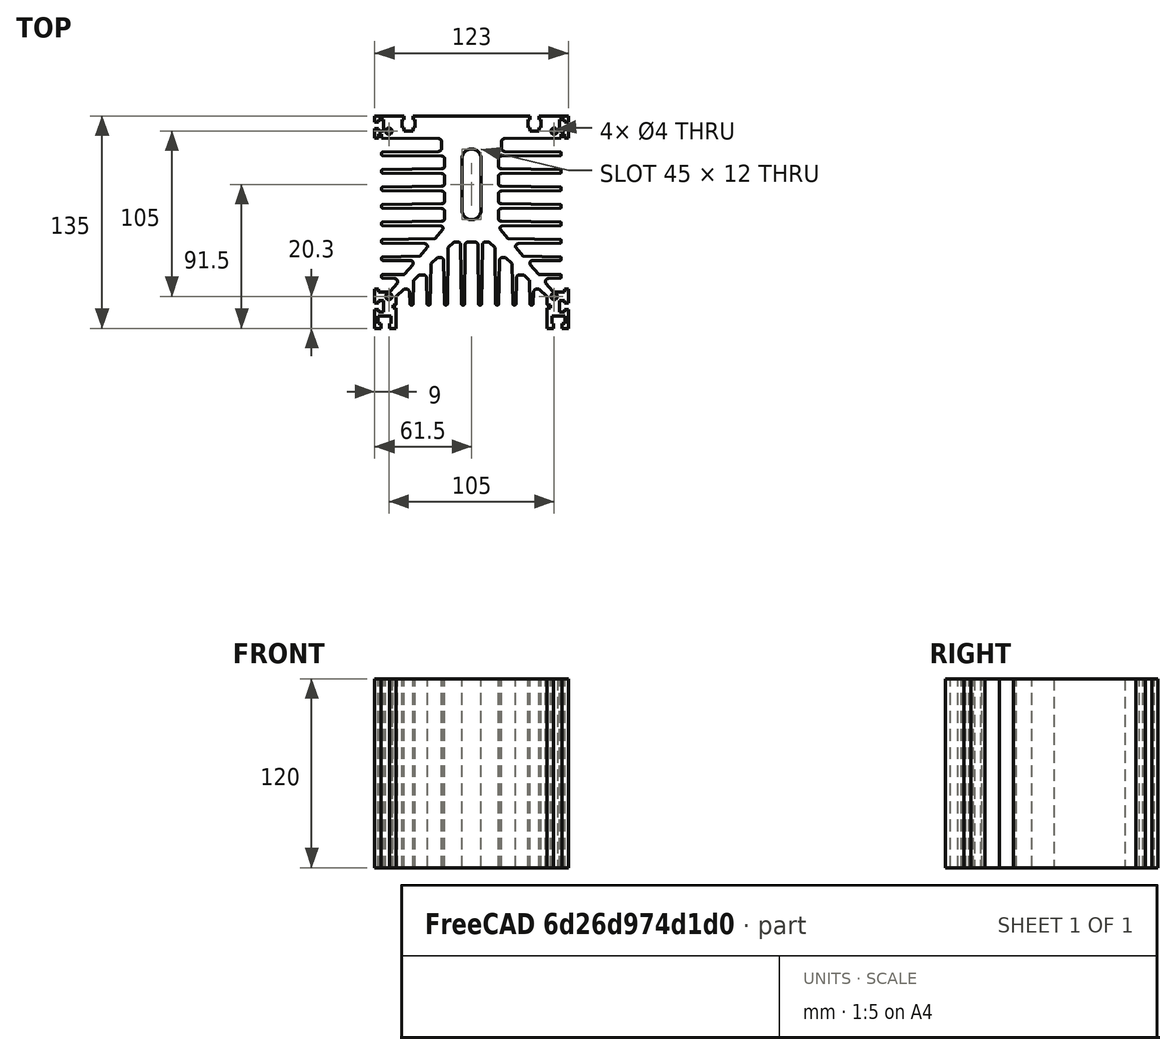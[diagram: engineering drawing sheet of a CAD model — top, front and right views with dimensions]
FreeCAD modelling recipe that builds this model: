
FCSTD DOCUMENT  (FreeCAD 0.17R13541 (Git))
Label: Heatsink RG07086
License: Other
LicenseURL: https://designlibre.org/license-en/
objects: Sketcher::SketchObject×1, PartDesign::Pad×1, PartDesign::Body×1, App::Part×1
note: 4 computed .brp shape members not serialized (recipe doc carries the construction recipe); baked Part::Feature solids carry a one-line shape summary decoded from their .brp

FEATURE [Sketcher::SketchObject] Sketch348
  sketch-geometry (348):
    g0: Circle CenterX=-52.5 CenterY=8.45 CenterZ=0 NormalX=0 NormalY=0 NormalZ=-1 AngleXU=0 Radius=2
    g1: ArcOfCircle CenterX=-56.6 CenterY=44.2243 CenterZ=0 NormalX=0 NormalY=0 NormalZ=1 AngleXU=0 Radius=0.4 StartAngle=1.58468 EndAngle=3.14159
    g2: ArcOfCircle CenterX=-56.6 CenterY=99.7552 CenterZ=0 NormalX=0 NormalY=0 NormalZ=1 AngleXU=0 Radius=0.4 StartAngle=1.58395 EndAngle=3.14159
    g3: ArcOfCircle CenterX=-32.9614 CenterY=34.5078 CenterZ=0 NormalX=0 NormalY=0 NormalZ=1 AngleXU=0 Radius=0.5 StartAngle=4.73298 EndAngle=5.5795
    g4: ArcOfCircle CenterX=-19.5 CenterY=51.6379 CenterZ=0 NormalX=0 NormalY=0 NormalZ=1 AngleXU=0 Radius=1.5 StartAngle=0 EndAngle=1.55798
    g5: ArcOfCircle CenterX=-56.6 CenterY=87.3325 CenterZ=0 NormalX=0 NormalY=0 NormalZ=1 AngleXU=0 Radius=0.4 StartAngle=3.14159 EndAngle=4.69989
    g6: ArcOfCircle CenterX=21 CenterY=106.676 CenterZ=0 NormalX=0 NormalY=0 NormalZ=1 AngleXU=0 Radius=2 StartAngle=1.58395 EndAngle=3.14159
    g7: ArcOfCircle CenterX=-19 CenterY=84.4623 CenterZ=0 NormalX=0 NormalY=0 NormalZ=1 AngleXU=0 Radius=2 StartAngle=0 EndAngle=1.5583
    g8: ArcOfCircle CenterX=0 CenterY=96.15 CenterZ=0 NormalX=0 NormalY=0 NormalZ=1 AngleXU=0 Radius=6 StartAngle=0 EndAngle=3.14159
    g9: ArcOfCircle CenterX=-21 CenterY=106.676 CenterZ=0 NormalX=0 NormalY=0 NormalZ=1 AngleXU=0 Radius=2 StartAngle=0 EndAngle=1.55764
    g10: ArcOfCircle CenterX=-19 CenterY=62.2498 CenterZ=0 NormalX=0 NormalY=0 NormalZ=1 AngleXU=0 Radius=2 StartAngle=0 EndAngle=1.5583
    g11: ArcOfCircle CenterX=-56.6 CenterY=66.4362 CenterZ=0 NormalX=0 NormalY=0 NormalZ=1 AngleXU=0 Radius=0.4 StartAngle=1.5833 EndAngle=3.14159
    g12: ArcOfCircle CenterX=-56.6 CenterY=33.1207 CenterZ=0 NormalX=0 NormalY=0 NormalZ=1 AngleXU=0 Radius=0.4 StartAngle=1.59139 EndAngle=3.14159
    g13: ArcOfCircle CenterX=-30 CenterY=40.0467 CenterZ=0 NormalX=0 NormalY=0 NormalZ=1 AngleXU=0 Radius=2 StartAngle=0 EndAngle=1.55356
    g14: ArcOfCircle CenterX=-19 CenterY=73.3561 CenterZ=0 NormalX=0 NormalY=0 NormalZ=1 AngleXU=0 Radius=2 StartAngle=0 EndAngle=1.5583
    g15: ArcOfCircle CenterX=-19 CenterY=95.5686 CenterZ=0 NormalX=0 NormalY=0 NormalZ=1 AngleXU=0 Radius=2 StartAngle=0 EndAngle=1.5583
    g16: ArcOfCircle CenterX=-56.6 CenterY=42.9057 CenterZ=0 NormalX=0 NormalY=0 NormalZ=1 AngleXU=0 Radius=0.4 StartAngle=3.14159 EndAngle=4.69515
    g17: ArcOfCircle CenterX=-56.6 CenterY=55.33 CenterZ=0 NormalX=0 NormalY=0 NormalZ=1 AngleXU=0 Radius=0.4 StartAngle=1.5833 EndAngle=3.14159
    g18: ArcOfCircle CenterX=-28.5 CenterY=39.765 CenterZ=0 NormalX=0 NormalY=0 NormalZ=1 AngleXU=0 Radius=0.5 StartAngle=5.5795 EndAngle=6.28319
    g19: ArcOfCircle CenterX=0 CenterY=63.15 CenterZ=0 NormalX=0 NormalY=0 NormalZ=1 AngleXU=0 Radius=6 StartAngle=3.14159 EndAngle=6.28319
    g20: ArcOfCircle CenterX=56.6 CenterY=99.7552 CenterZ=0 NormalX=0 NormalY=0 NormalZ=1 AngleXU=0 Radius=0.4 StartAngle=0 EndAngle=1.55764
    g21: ArcOfCircle CenterX=-21 CenterY=102.624 CenterZ=0 NormalX=0 NormalY=0 NormalZ=1 AngleXU=0 Radius=2 StartAngle=4.72555 EndAngle=6.28319
    g22: ArcOfCircle CenterX=-56.6 CenterY=65.12 CenterZ=0 NormalX=0 NormalY=0 NormalZ=1 AngleXU=0 Radius=0.4 StartAngle=3.14159 EndAngle=4.69989
    g23: ArcOfCircle CenterX=-18.5 CenterY=51.5489 CenterZ=0 NormalX=0 NormalY=0 NormalZ=1 AngleXU=0 Radius=0.5 StartAngle=5.5795 EndAngle=6.28319
    g24: ArcOfCircle CenterX=-23.5626 CenterY=45.5832 CenterZ=0 NormalX=0 NormalY=0 NormalZ=1 AngleXU=0 Radius=0.5 StartAngle=4.72628 EndAngle=5.5795
    g25: ArcOfCircle CenterX=-56.6 CenterY=54.0137 CenterZ=0 NormalX=0 NormalY=0 NormalZ=1 AngleXU=0 Radius=0.4 StartAngle=3.14159 EndAngle=4.69957
    g26: ArcOfCircle CenterX=-19 CenterY=69.3064 CenterZ=0 NormalX=0 NormalY=0 NormalZ=1 AngleXU=0 Radius=2 StartAngle=4.72489 EndAngle=6.28319
    g27: ArcOfCircle CenterX=-56.6 CenterY=98.4388 CenterZ=0 NormalX=0 NormalY=0 NormalZ=1 AngleXU=0 Radius=0.4 StartAngle=3.14159 EndAngle=4.69989
    g28: ArcOfCircle CenterX=-56.6 CenterY=77.5425 CenterZ=0 NormalX=0 NormalY=0 NormalZ=1 AngleXU=0 Radius=0.4 StartAngle=1.5833 EndAngle=3.14159
    g29: ArcOfCircle CenterX=21 CenterY=102.624 CenterZ=0 NormalX=0 NormalY=0 NormalZ=1 AngleXU=0 Radius=2 StartAngle=3.14159 EndAngle=4.69923
    g30: ArcOfCircle CenterX=-19 CenterY=58.2002 CenterZ=0 NormalX=0 NormalY=0 NormalZ=1 AngleXU=0 Radius=2 StartAngle=4.72489 EndAngle=6.28319
    g31: ArcOfCircle CenterX=-56.6 CenterY=76.2263 CenterZ=0 NormalX=0 NormalY=0 NormalZ=1 AngleXU=0 Radius=0.4 StartAngle=3.14159 EndAngle=4.69989
    g32: ArcOfCircle CenterX=-19 CenterY=80.4127 CenterZ=0 NormalX=0 NormalY=0 NormalZ=1 AngleXU=0 Radius=2 StartAngle=4.72489 EndAngle=6.28319
    g33: ArcOfCircle CenterX=-19 CenterY=91.5189 CenterZ=0 NormalX=0 NormalY=0 NormalZ=1 AngleXU=0 Radius=2 StartAngle=4.72489 EndAngle=6.28319
    g34: ArcOfCircle CenterX=-56.6 CenterY=88.6487 CenterZ=0 NormalX=0 NormalY=0 NormalZ=1 AngleXU=0 Radius=0.4 StartAngle=1.5833 EndAngle=3.14159
    g35: LineSegment StartX=17 StartY=73.3561 StartZ=0 EndX=17 EndY=69.3064 EndZ=0
    g36: LineSegment StartX=18.975 StartY=89.5191 StartZ=0 EndX=56.605 EndY=89.0487 EndZ=0
    g37: LineSegment StartX=56.605 StartY=75.8263 StartZ=0 EndX=18.975 EndY=75.3559 EndZ=0
    g38: LineSegment StartX=56.605 StartY=64.7201 StartZ=0 EndX=18.975 EndY=64.2497 EndZ=0
    g39: LineSegment StartX=56.605 StartY=86.9326 StartZ=0 EndX=18.975 EndY=86.4622 EndZ=0
    g40: LineSegment StartX=17 StartY=84.4623 StartZ=0 EndX=17 EndY=80.4127 EndZ=0
    g41: LineSegment StartX=17 StartY=95.5686 StartZ=0 EndX=17 EndY=91.5189 EndZ=0
    g42: LineSegment StartX=18.975 StartY=78.4128 StartZ=0 EndX=56.605 EndY=77.9424 EndZ=0
    g43: Circle CenterX=52.5 CenterY=8.45 CenterZ=0 NormalX=0 NormalY=0 NormalZ=-1 AngleXU=0 Radius=2
    g44: Circle CenterX=-52.5 CenterY=113.45 CenterZ=0 NormalX=0 NormalY=0 NormalZ=-1 AngleXU=0 Radius=2
    g45: LineSegment StartX=18.975 StartY=67.3066 StartZ=0 EndX=56.605 EndY=66.8362 EndZ=0
    g46: LineSegment StartX=56.605 StartY=98.0388 StartZ=0 EndX=18.975 EndY=97.5684 EndZ=0
    g47: LineSegment StartX=57.5 StartY=-11.85 StartZ=0 EndX=61.5 EndY=-11.85 EndZ=0
    g48: Circle CenterX=52.5 CenterY=113.45 CenterZ=0 NormalX=0 NormalY=0 NormalZ=-1 AngleXU=0 Radius=2
    g49: LineSegment StartX=48.4 StartY=3.15 StartZ=0 EndX=50 EndY=3.15 EndZ=0
    g50: LineSegment StartX=48 StartY=3.55 StartZ=0 EndX=48 EndY=7.93471 EndZ=0
    g51: LineSegment StartX=42.5153 StartY=13.15 StartZ=0 EndX=41.4025 EndY=13.15 EndZ=0
    g52: LineSegment StartX=51 StartY=-8.85 StartZ=0 EndX=52 EndY=-8.85 EndZ=0
    g53: LineSegment StartX=57.5 StartY=-8.85 StartZ=0 EndX=59.4 EndY=-8.85 EndZ=0
    g54: LineSegment StartX=39.019 StartY=3.53002 StartZ=0 EndX=39.405 EndY=11.2499 EndZ=0
    g55: LineSegment StartX=52 StartY=-11.85 StartZ=0 EndX=48 EndY=-11.85 EndZ=0
    g56: LineSegment StartX=59 StartY=0 StartZ=0 EndX=59 EndY=-1.55 EndZ=0
    g57: LineSegment StartX=56 StartY=-1.55 StartZ=0 EndX=56 EndY=5.85 EndZ=0
    g58: LineSegment StartX=42.8589 StartY=13.0132 StartZ=0 EndX=47.8436 EndY=8.29795 EndZ=0
    g59: LineSegment StartX=56 StartY=5.85 StartZ=0 EndX=59 EndY=5.85 EndZ=0
    g60: LineSegment StartX=61.5 StartY=0 StartZ=0 EndX=59 EndY=0 EndZ=0
    g61: LineSegment StartX=61.5 StartY=-11.85 StartZ=0 EndX=61.5 EndY=0 EndZ=0
    g62: LineSegment StartX=51 StartY=-3.85 StartZ=0 EndX=51 EndY=-8.85 EndZ=0
    g63: LineSegment StartX=57.5 StartY=-11.85 StartZ=0 EndX=57.5 EndY=-8.85 EndZ=0
    g64: LineSegment StartX=48 StartY=1.15 StartZ=0 EndX=50 EndY=1.15 EndZ=0
    g65: LineSegment StartX=59.4 StartY=-3.85 StartZ=0 EndX=51 EndY=-3.85 EndZ=0
    g66: LineSegment StartX=48 StartY=-11.85 StartZ=0 EndX=48 EndY=1.15 EndZ=0
    g67: LineSegment StartX=59.4 StartY=-8.85 StartZ=0 EndX=59.4 EndY=-3.85 EndZ=0
    g68: LineSegment StartX=50 StartY=1.15 StartZ=0 EndX=50 EndY=3.15 EndZ=0
    g69: LineSegment StartX=59 StartY=-1.55 StartZ=0 EndX=56 EndY=-1.55 EndZ=0
    g70: LineSegment StartX=52 StartY=-8.85 StartZ=0 EndX=52 EndY=-11.85 EndZ=0
    g71: LineSegment StartX=36.7179 StartY=18.62 StartZ=0 EndX=37.1148 EndY=3.53948 EndZ=0
    g72: LineSegment StartX=-11.1446 StartY=43.0132 StartZ=0 EndX=-14.8812 EndY=39.4786 EndZ=0
    g73: LineSegment StartX=11.1446 StartY=43.0132 StartZ=0 EndX=14.8812 EndY=39.4786 EndZ=0
    g74: LineSegment StartX=-2.02484 StartY=43.15 StartZ=0 EndX=2.02484 EndY=43.15 EndZ=0
    g75: LineSegment StartX=28.5738 StartY=20.2026 StartZ=0 EndX=28.1352 EndY=3.53948 EndZ=0
    g76: LineSegment StartX=-6.96924 StartY=41.1812 StartZ=0 EndX=-6.38115 EndY=3.54375 EndZ=0
    g77: LineSegment StartX=6.96924 StartY=41.1812 StartZ=0 EndX=6.38115 EndY=3.54375 EndZ=0
    g78: LineSegment StartX=4.02469 StartY=41.175 StartZ=0 EndX=4.49506 EndY=3.545 EndZ=0
    g79: LineSegment StartX=-4.02469 StartY=41.175 StartZ=0 EndX=-4.49506 EndY=3.545 EndZ=0
    g80: LineSegment StartX=-15.0375 StartY=39.1201 StartZ=0 EndX=-15.3713 EndY=3.54625 EndZ=0
    g81: LineSegment StartX=17.7172 StartY=31.1833 StartZ=0 EndX=17.2566 EndY=3.54333 EndZ=0
    g82: LineSegment StartX=25.7845 StartY=28.9584 StartZ=0 EndX=26.2429 EndY=3.54279 EndZ=0
    g83: LineSegment StartX=-21.3724 StartY=33.15 StartZ=0 EndX=-19.7169 EndY=33.15 EndZ=0
    g84: LineSegment StartX=-17.7172 StartY=31.1833 StartZ=0 EndX=-17.2566 EndY=3.54333 EndZ=0
    g85: LineSegment StartX=8.96899 StartY=43.15 StartZ=0 EndX=10.801 EndY=43.15 EndZ=0
    g86: LineSegment StartX=30.5731 StartY=22.15 StartZ=0 EndX=33.001 EndY=22.15 EndZ=0
    g87: LineSegment StartX=-8.96899 StartY=43.15 StartZ=0 EndX=-10.801 EndY=43.15 EndZ=0
    g88: LineSegment StartX=61.5 StartY=4.3 StartZ=0 EndX=61.5 EndY=13.3 EndZ=0
    g89: LineSegment StartX=15.0375 StartY=39.1201 StartZ=0 EndX=15.3713 EndY=3.54625 EndZ=0
    g90: LineSegment StartX=21.3724 StartY=33.15 StartZ=0 EndX=19.7169 EndY=33.15 EndZ=0
    g91: LineSegment StartX=-21.716 StartY=33.0132 StartZ=0 EndX=-25.6281 EndY=29.3126 EndZ=0
    g92: LineSegment StartX=21.716 StartY=33.0132 StartZ=0 EndX=25.6281 EndY=29.3126 EndZ=0
    g93: LineSegment StartX=-25.7845 StartY=28.9584 StartZ=0 EndX=-26.2429 EndY=3.54279 EndZ=0
    g94: LineSegment StartX=33.3446 StartY=22.0132 StartZ=0 EndX=36.5617 EndY=18.97 EndZ=0
    g95: LineSegment StartX=47.1188 StartY=17.052 StartZ=0 EndX=51.8502 EndY=11.4765 EndZ=0
    g96: LineSegment StartX=23.5556 StartY=45.0833 StartZ=0 EndX=56.6056 EndY=44.6242 EndZ=0
    g97: LineSegment StartX=18 StartY=51.6379 StartZ=0 EndX=18 EndY=51.5489 EndZ=0
    g98: LineSegment StartX=57 StartY=22.0063 StartZ=0 EndX=57 EndY=20.6805 EndZ=0
    g99: LineSegment StartX=59 StartY=4.3 StartZ=0 EndX=61.5 EndY=4.3 EndZ=0
    g100: LineSegment StartX=37 StartY=29.4062 StartZ=0 EndX=37 EndY=29.1595 EndZ=0
    g101: LineSegment StartX=59 StartY=5.85 StartZ=0 EndX=59 EndY=4.3 EndZ=0
    g102: LineSegment StartX=56.6051 StartY=53.6137 StartZ=0 EndX=19.4808 EndY=53.1377 EndZ=0
    g103: LineSegment StartX=42.8066 StartY=22.4062 StartZ=0 EndX=56.6 EndY=22.4062 EndZ=0
    g104: LineSegment StartX=56.6069 StartY=42.5057 StartZ=0 EndX=29.9655 EndY=42.0464 EndZ=0
    g105: LineSegment StartX=28.1188 StartY=39.4415 StartZ=0 EndX=32.5801 EndY=34.1842 EndZ=0
    g106: LineSegment StartX=37.1188 StartY=28.8359 StartZ=0 EndX=42.4253 EndY=22.5827 EndZ=0
    g107: LineSegment StartX=28 StartY=40.0467 StartZ=0 EndX=28 EndY=39.765 EndZ=0
    g108: LineSegment StartX=56.6 StartY=31.4062 StartZ=0 EndX=39 EndY=31.4062 EndZ=0
    g109: LineSegment StartX=56.62 StartY=20.281 StartZ=0 EndX=48.9001 EndY=19.895 EndZ=0
    g110: LineSegment StartX=18.1188 StartY=51.2254 StartZ=0 EndX=23.1814 EndY=45.2597 EndZ=0
    g111: LineSegment StartX=61.5 StartY=13.3 StartZ=0 EndX=59 EndY=13.3 EndZ=0
    g112: LineSegment StartX=47 StartY=17.8975 StartZ=0 EndX=47 EndY=17.3755 EndZ=0
    g113: LineSegment StartX=59 StartY=13.3 StartZ=0 EndX=59 EndY=11.3 EndZ=0
    g114: LineSegment StartX=-59.4 StartY=-8.85 StartZ=0 EndX=-59.4 EndY=-3.85 EndZ=0
    g115: LineSegment StartX=18.975 StartY=56.2003 StartZ=0 EndX=56.605 EndY=55.7299 EndZ=0
    g116: LineSegment StartX=32.9511 StartY=34.0079 StartZ=0 EndX=56.6082 EndY=33.5206 EndZ=0
    g117: LineSegment StartX=59 StartY=11.3 StartZ=0 EndX=52.2315 EndY=11.3 EndZ=0
    g118: LineSegment StartX=-59 StartY=0 StartZ=0 EndX=-59 EndY=-1.55 EndZ=0
    g119: LineSegment StartX=-51 StartY=-3.85 StartZ=0 EndX=-51 EndY=-8.85 EndZ=0
    g120: LineSegment StartX=-61.5 StartY=-11.85 StartZ=0 EndX=-61.5 EndY=0 EndZ=0
    g121: LineSegment StartX=-42.5153 StartY=13.15 StartZ=0 EndX=-41.4025 EndY=13.15 EndZ=0
    g122: LineSegment StartX=-51 StartY=-8.85 StartZ=0 EndX=-52 EndY=-8.85 EndZ=0
    g123: LineSegment StartX=-52 StartY=-11.85 StartZ=0 EndX=-48 EndY=-11.85 EndZ=0
    g124: LineSegment StartX=-57.5 StartY=-11.85 StartZ=0 EndX=-57.5 EndY=-8.85 EndZ=0
    g125: LineSegment StartX=-61.5 StartY=0 StartZ=0 EndX=-59 EndY=0 EndZ=0
    g126: LineSegment StartX=-28.5738 StartY=20.2026 StartZ=0 EndX=-28.1352 EndY=3.53948 EndZ=0
    g127: LineSegment StartX=-39.019 StartY=3.53002 StartZ=0 EndX=-39.405 EndY=11.2499 EndZ=0
    g128: LineSegment StartX=-50 StartY=1.15 StartZ=0 EndX=-50 EndY=3.15 EndZ=0
    g129: LineSegment StartX=-57.5 StartY=-8.85 StartZ=0 EndX=-59.4 EndY=-8.85 EndZ=0
    g130: LineSegment StartX=-33.3446 StartY=22.0132 StartZ=0 EndX=-36.5617 EndY=18.97 EndZ=0
    g131: LineSegment StartX=-42.8589 StartY=13.0132 StartZ=0 EndX=-47.8436 EndY=8.29795 EndZ=0
    g132: LineSegment StartX=-48 StartY=3.55 StartZ=0 EndX=-48 EndY=7.93471 EndZ=0
    g133: LineSegment StartX=-48 StartY=-11.85 StartZ=0 EndX=-48 EndY=1.15 EndZ=0
    g134: LineSegment StartX=-36.7179 StartY=18.62 StartZ=0 EndX=-37.1148 EndY=3.53948 EndZ=0
    g135: LineSegment StartX=-52 StartY=-8.85 StartZ=0 EndX=-52 EndY=-11.85 EndZ=0
    g136: LineSegment StartX=-48 StartY=1.15 StartZ=0 EndX=-50 EndY=1.15 EndZ=0
    g137: LineSegment StartX=-33.001 StartY=22.15 StartZ=0 EndX=-30.5731 EndY=22.15 EndZ=0
    g138: LineSegment StartX=-57.5 StartY=-11.85 StartZ=0 EndX=-61.5 EndY=-11.85 EndZ=0
    g139: LineSegment StartX=-59.4 StartY=-3.85 StartZ=0 EndX=-51 EndY=-3.85 EndZ=0
    g140: LineSegment StartX=-29.9655 StartY=42.0464 StartZ=0 EndX=-56.6069 EndY=42.5057 EndZ=0
    g141: LineSegment StartX=-61.5 StartY=13.3 StartZ=0 EndX=-59 EndY=13.3 EndZ=0
    g142: LineSegment StartX=-56.6056 StartY=44.6242 StartZ=0 EndX=-23.5556 EndY=45.0833 EndZ=0
    g143: LineSegment StartX=-56 StartY=-1.55 StartZ=0 EndX=-56 EndY=5.85 EndZ=0
    g144: LineSegment StartX=-59 StartY=4.3 StartZ=0 EndX=-61.5 EndY=4.3 EndZ=0
    g145: LineSegment StartX=-48.9001 StartY=19.895 StartZ=0 EndX=-56.62 EndY=20.281 EndZ=0
    g146: LineSegment StartX=-51.8502 StartY=11.4765 StartZ=0 EndX=-47.1188 EndY=17.052 EndZ=0
    g147: LineSegment StartX=-37 StartY=29.1595 StartZ=0 EndX=-37 EndY=29.4062 EndZ=0
    g148: LineSegment StartX=-23.1814 StartY=45.2597 StartZ=0 EndX=-18.1188 EndY=51.2254 EndZ=0
    g149: LineSegment StartX=-32.5801 StartY=34.1842 StartZ=0 EndX=-28.1188 EndY=39.4415 EndZ=0
    g150: LineSegment StartX=-42.4253 StartY=22.5827 StartZ=0 EndX=-37.1188 EndY=28.8359 EndZ=0
    g151: LineSegment StartX=-56.6 StartY=22.4062 StartZ=0 EndX=-42.8066 EndY=22.4062 EndZ=0
    g152: LineSegment StartX=-59 StartY=-1.55 StartZ=0 EndX=-56 EndY=-1.55 EndZ=0
    g153: LineSegment StartX=-59 StartY=11.3 StartZ=0 EndX=-52.2315 EndY=11.3 EndZ=0
    g154: LineSegment StartX=-56 StartY=5.85 StartZ=0 EndX=-59 EndY=5.85 EndZ=0
    g155: LineSegment StartX=-61.5 StartY=4.3 StartZ=0 EndX=-61.5 EndY=13.3 EndZ=0
    g156: LineSegment StartX=-59 StartY=13.3 StartZ=0 EndX=-59 EndY=11.3 EndZ=0
    g157: LineSegment StartX=-57 StartY=22.0063 StartZ=0 EndX=-57 EndY=20.6805 EndZ=0
    g158: LineSegment StartX=-59 StartY=5.85 StartZ=0 EndX=-59 EndY=4.3 EndZ=0
    g159: LineSegment StartX=-56.605 StartY=89.0487 StartZ=0 EndX=-18.975 EndY=89.5191 EndZ=0
    g160: LineSegment StartX=-47 StartY=17.3755 StartZ=0 EndX=-47 EndY=17.8975 EndZ=0
    g161: LineSegment StartX=-39 StartY=31.4062 StartZ=0 EndX=-56.6 EndY=31.4062 EndZ=0
    g162: LineSegment StartX=-28 StartY=39.765 StartZ=0 EndX=-28 EndY=40.0467 EndZ=0
    g163: LineSegment StartX=-56.605 StartY=77.9424 StartZ=0 EndX=-18.975 EndY=78.4128 EndZ=0
    g164: LineSegment StartX=-56.6082 StartY=33.5206 StartZ=0 EndX=-32.9511 EndY=34.0079 EndZ=0
    g165: LineSegment StartX=-59 StartY=111.45 StartZ=0 EndX=-57 EndY=111.45 EndZ=0
    g166: LineSegment StartX=-61.5 StartY=115 StartZ=0 EndX=-61.5 EndY=109.15 EndZ=0
    g167: LineSegment StartX=-18 StartY=51.5489 StartZ=0 EndX=-18 EndY=51.6379 EndZ=0
    g168: LineSegment StartX=-19.4808 StartY=53.1377 StartZ=0 EndX=-56.6051 EndY=53.6137 EndZ=0
    g169: LineSegment StartX=-59 StartY=115 StartZ=0 EndX=-61.5 EndY=115 EndZ=0
    g170: LineSegment StartX=-61.5 StartY=109.15 StartZ=0 EndX=-59 EndY=109.15 EndZ=0
    g171: LineSegment StartX=-18.975 StartY=64.2497 StartZ=0 EndX=-56.605 EndY=64.7201 EndZ=0
    g172: LineSegment StartX=-56.605 StartY=66.8362 StartZ=0 EndX=-18.975 EndY=67.3066 EndZ=0
    g173: LineSegment StartX=-59 StartY=113.45 StartZ=0 EndX=-59 EndY=115 EndZ=0
    g174: LineSegment StartX=-59 StartY=109.15 StartZ=0 EndX=-59 EndY=111.45 EndZ=0
    g175: LineSegment StartX=-19 StartY=102.624 StartZ=0 EndX=-19 EndY=106.676 EndZ=0
    g176: LineSegment StartX=-56.605 StartY=55.7299 StartZ=0 EndX=-18.975 EndY=56.2003 EndZ=0
    g177: LineSegment StartX=-17 StartY=58.2002 StartZ=0 EndX=-17 EndY=62.2498 EndZ=0
    g178: LineSegment StartX=-17 StartY=91.5189 StartZ=0 EndX=-17 EndY=95.5686 EndZ=0
    g179: LineSegment StartX=-17 StartY=80.4127 StartZ=0 EndX=-17 EndY=84.4623 EndZ=0
    g180: LineSegment StartX=-20.9737 StartY=108.676 StartZ=0 EndX=-57 EndY=109.15 EndZ=0
    g181: LineSegment StartX=-18.975 StartY=75.3559 StartZ=0 EndX=-56.605 EndY=75.8263 EndZ=0
    g182: LineSegment StartX=-18.975 StartY=86.4622 StartZ=0 EndX=-56.605 EndY=86.9326 EndZ=0
    g183: LineSegment StartX=-35.8 StartY=120.85 StartZ=0 EndX=-37.25 EndY=120.85 EndZ=0
    g184: LineSegment StartX=-56.6053 StartY=100.155 StartZ=0 EndX=-20.9737 EndY=100.624 EndZ=0
    g185: LineSegment StartX=-18.975 StartY=97.5684 StartZ=0 EndX=-56.605 EndY=98.0388 EndZ=0
    g186: LineSegment StartX=35.8 StartY=120.85 StartZ=0 EndX=37.25 EndY=120.85 EndZ=0
    g187: LineSegment StartX=-17 StartY=69.3064 StartZ=0 EndX=-17 EndY=73.3561 EndZ=0
    g188: LineSegment StartX=-42.75 StartY=115.85 StartZ=0 EndX=-42.75 EndY=113.45 EndZ=0
    g189: LineSegment StartX=-44.2 StartY=115.85 StartZ=0 EndX=-42.75 EndY=115.85 EndZ=0
    g190: LineSegment StartX=-59 StartY=120.85 StartZ=0 EndX=-56 EndY=120.85 EndZ=0
    g191: LineSegment StartX=-61.5 StartY=123.15 StartZ=0 EndX=-61.5 EndY=119.3 EndZ=0
    g192: LineSegment StartX=-61.5 StartY=123.15 StartZ=0 EndX=-42.75 EndY=123.15 EndZ=0
    g193: LineSegment StartX=37.25 StartY=115.85 StartZ=0 EndX=35.8 EndY=115.85 EndZ=0
    g194: LineSegment StartX=-56 StartY=120.85 StartZ=0 EndX=-56 EndY=113.45 EndZ=0
    g195: LineSegment StartX=35.8 StartY=115.85 StartZ=0 EndX=35.8 EndY=120.85 EndZ=0
    g196: LineSegment StartX=-37.25 StartY=120.85 StartZ=0 EndX=-37.25 EndY=123.15 EndZ=0
    g197: LineSegment StartX=-42.75 StartY=120.85 StartZ=0 EndX=-44.2 EndY=120.85 EndZ=0
    g198: LineSegment StartX=37.25 StartY=120.85 StartZ=0 EndX=37.25 EndY=123.15 EndZ=0
    g199: LineSegment StartX=-44.2 StartY=120.85 StartZ=0 EndX=-44.2 EndY=115.85 EndZ=0
    g200: LineSegment StartX=-37.25 StartY=115.85 StartZ=0 EndX=-35.8 EndY=115.85 EndZ=0
    g201: LineSegment StartX=-42.75 StartY=113.45 StartZ=0 EndX=-37.25 EndY=113.45 EndZ=0
    g202: LineSegment StartX=-61.5 StartY=119.3 StartZ=0 EndX=-59 EndY=119.3 EndZ=0
    g203: LineSegment StartX=37.25 StartY=123.15 StartZ=0 EndX=-37.25 EndY=123.15 EndZ=0
    g204: LineSegment StartX=-56 StartY=113.45 StartZ=0 EndX=-59 EndY=113.45 EndZ=0
    g205: LineSegment StartX=-42.75 StartY=123.15 StartZ=0 EndX=-42.75 EndY=120.85 EndZ=0
    g206: LineSegment StartX=-37.25 StartY=113.45 StartZ=0 EndX=-37.25 EndY=115.85 EndZ=0
    g207: LineSegment StartX=-59 StartY=119.3 StartZ=0 EndX=-59 EndY=120.85 EndZ=0
    g208: LineSegment StartX=42.75 StartY=113.45 StartZ=0 EndX=37.25 EndY=113.45 EndZ=0
    g209: LineSegment StartX=61.5 StartY=123.15 StartZ=0 EndX=61.5 EndY=119.3 EndZ=0
    g210: LineSegment StartX=19 StartY=106.676 StartZ=0 EndX=19 EndY=102.624 EndZ=0
    g211: LineSegment StartX=-35.8 StartY=115.85 StartZ=0 EndX=-35.8 EndY=120.85 EndZ=0
    g212: LineSegment StartX=59 StartY=109.15 StartZ=0 EndX=59 EndY=111.45 EndZ=0
    g213: LineSegment StartX=20.9737 StartY=100.624 StartZ=0 EndX=56.6053 EndY=100.155 EndZ=0
    g214: LineSegment StartX=56 StartY=113.45 StartZ=0 EndX=59 EndY=113.45 EndZ=0
    g215: LineSegment StartX=59 StartY=119.3 StartZ=0 EndX=59 EndY=120.85 EndZ=0
    g216: LineSegment StartX=61.5 StartY=123.15 StartZ=0 EndX=42.75 EndY=123.15 EndZ=0
    g217: LineSegment StartX=59 StartY=113.45 StartZ=0 EndX=59 EndY=115 EndZ=0
    g218: LineSegment StartX=61.5 StartY=119.3 StartZ=0 EndX=59 EndY=119.3 EndZ=0
    g219: LineSegment StartX=56 StartY=120.85 StartZ=0 EndX=56 EndY=113.45 EndZ=0
    g220: LineSegment StartX=42.75 StartY=120.85 StartZ=0 EndX=44.2 EndY=120.85 EndZ=0
    g221: LineSegment StartX=37.25 StartY=113.45 StartZ=0 EndX=37.25 EndY=115.85 EndZ=0
    g222: LineSegment StartX=61.5 StartY=109.15 StartZ=0 EndX=59 EndY=109.15 EndZ=0
    g223: LineSegment StartX=42.75 StartY=123.15 StartZ=0 EndX=42.75 EndY=120.85 EndZ=0
    g224: LineSegment StartX=44.2 StartY=120.85 StartZ=0 EndX=44.2 EndY=115.85 EndZ=0
    g225: LineSegment StartX=57 StartY=109.15 StartZ=0 EndX=20.9737 EndY=108.676 EndZ=0
    g226: LineSegment StartX=59 StartY=111.45 StartZ=0 EndX=57 EndY=111.45 EndZ=0
    g227: LineSegment StartX=59 StartY=120.85 StartZ=0 EndX=56 EndY=120.85 EndZ=0
    g228: LineSegment StartX=61.5 StartY=115 StartZ=0 EndX=61.5 EndY=109.15 EndZ=0
    g229: LineSegment StartX=59 StartY=115 StartZ=0 EndX=61.5 EndY=115 EndZ=0
    g230: LineSegment StartX=42.75 StartY=115.85 StartZ=0 EndX=42.75 EndY=113.45 EndZ=0
    g231: LineSegment StartX=44.2 StartY=115.85 StartZ=0 EndX=42.75 EndY=115.85 EndZ=0
    g232: LineSegment StartX=-57 StartY=88.6487 StartZ=0 EndX=-57 EndY=87.3325 EndZ=0
    g233: LineSegment StartX=-57 StartY=111.45 StartZ=0 EndX=-57 EndY=109.15 EndZ=0
    g234: LineSegment StartX=57 StartY=66.4362 StartZ=0 EndX=57 EndY=65.12 EndZ=0
    g235: LineSegment StartX=26.6428 StartY=3.15 StartZ=0 EndX=27.7354 EndY=3.15 EndZ=0
    g236: LineSegment StartX=-27.7354 StartY=3.15 StartZ=0 EndX=-26.6428 EndY=3.15 EndZ=0
    g237: LineSegment StartX=37.5146 StartY=3.15 StartZ=0 EndX=38.6195 EndY=3.15 EndZ=0
    g238: LineSegment StartX=57 StartY=111.45 StartZ=0 EndX=57 EndY=109.15 EndZ=0
    g239: LineSegment StartX=57 StartY=55.33 StartZ=0 EndX=57 EndY=54.0137 EndZ=0
    g240: LineSegment StartX=4.89503 StartY=3.15 StartZ=0 EndX=5.9812 EndY=3.15 EndZ=0
    g241: LineSegment StartX=57 StartY=44.2243 StartZ=0 EndX=57 EndY=42.9057 EndZ=0
    g242: LineSegment StartX=-6 StartY=96.15 StartZ=0 EndX=-6 EndY=63.15 EndZ=0
    g243: LineSegment StartX=15.7713 StartY=3.15 StartZ=0 EndX=16.8566 EndY=3.15 EndZ=0
    g244: LineSegment StartX=-38.6195 StartY=3.15 StartZ=0 EndX=-37.5146 EndY=3.15 EndZ=0
    g245: LineSegment StartX=-16.8566 StartY=3.15 StartZ=0 EndX=-15.7713 EndY=3.15 EndZ=0
    g246: LineSegment StartX=-57 StartY=55.33 StartZ=0 EndX=-57 EndY=54.0137 EndZ=0
    g247: LineSegment StartX=-57 StartY=77.5425 StartZ=0 EndX=-57 EndY=76.2263 EndZ=0
    g248: LineSegment StartX=-50 StartY=3.15 StartZ=0 EndX=-48.4 EndY=3.15 EndZ=0
    g249: LineSegment StartX=-57 StartY=44.2243 StartZ=0 EndX=-57 EndY=42.9057 EndZ=0
    g250: LineSegment StartX=-57 StartY=66.4362 StartZ=0 EndX=-57 EndY=65.12 EndZ=0
    g251: LineSegment StartX=-5.9812 StartY=3.15 StartZ=0 EndX=-4.89503 EndY=3.15 EndZ=0
    g252: LineSegment StartX=6 StartY=63.15 StartZ=0 EndX=6 EndY=96.15 EndZ=0
    g253: LineSegment StartX=-57 StartY=33.1207 StartZ=0 EndX=-57 EndY=31.8062 EndZ=0
    g254: LineSegment StartX=-57 StartY=99.7552 StartZ=0 EndX=-57 EndY=98.4388 EndZ=0
    g255: LineSegment StartX=57 StartY=77.5425 StartZ=0 EndX=57 EndY=76.2263 EndZ=0
    g256: ArcOfCircle CenterX=19 CenterY=73.3561 CenterZ=0 NormalX=0 NormalY=0 NormalZ=1 AngleXU=0 Radius=2 StartAngle=1.5833 EndAngle=3.14159
    g257: ArcOfCircle CenterX=19.5 CenterY=51.6379 CenterZ=0 NormalX=0 NormalY=0 NormalZ=1 AngleXU=0 Radius=1.5 StartAngle=1.58362 EndAngle=3.14159
    g258: ArcOfCircle CenterX=19 CenterY=62.2498 CenterZ=0 NormalX=0 NormalY=0 NormalZ=1 AngleXU=0 Radius=2 StartAngle=1.5833 EndAngle=3.14159
    g259: ArcOfCircle CenterX=56.6 CenterY=65.12 CenterZ=0 NormalX=0 NormalY=0 NormalZ=1 AngleXU=0 Radius=0.4 StartAngle=4.72489 EndAngle=6.28319
    g260: ArcOfCircle CenterX=19 CenterY=91.5189 CenterZ=0 NormalX=0 NormalY=0 NormalZ=1 AngleXU=0 Radius=2 StartAngle=3.14159 EndAngle=4.69989
    g261: ArcOfCircle CenterX=56.6 CenterY=66.4362 CenterZ=0 NormalX=0 NormalY=0 NormalZ=1 AngleXU=0 Radius=0.4 StartAngle=0 EndAngle=1.5583
    g262: ArcOfCircle CenterX=56.6 CenterY=54.0137 CenterZ=0 NormalX=0 NormalY=0 NormalZ=1 AngleXU=0 Radius=0.4 StartAngle=4.72521 EndAngle=6.28319
    g263: LineSegment StartX=57 StartY=99.7552 StartZ=0 EndX=57 EndY=98.4388 EndZ=0
    g264: ArcOfCircle CenterX=56.6 CenterY=87.3325 CenterZ=0 NormalX=0 NormalY=0 NormalZ=1 AngleXU=0 Radius=0.4 StartAngle=4.72489 EndAngle=6.28319
    g265: LineSegment StartX=57 StartY=33.1207 StartZ=0 EndX=57 EndY=31.8062 EndZ=0
    g266: ArcOfCircle CenterX=19 CenterY=69.3064 CenterZ=0 NormalX=0 NormalY=0 NormalZ=1 AngleXU=0 Radius=2 StartAngle=3.14159 EndAngle=4.69989
    g267: ArcOfCircle CenterX=18.5 CenterY=51.5489 CenterZ=0 NormalX=0 NormalY=0 NormalZ=1 AngleXU=0 Radius=0.5 StartAngle=3.14159 EndAngle=3.84528
    g268: ArcOfCircle CenterX=19 CenterY=58.2002 CenterZ=0 NormalX=0 NormalY=0 NormalZ=1 AngleXU=0 Radius=2 StartAngle=3.14159 EndAngle=4.69989
    g269: ArcOfCircle CenterX=56.6 CenterY=98.4388 CenterZ=0 NormalX=0 NormalY=0 NormalZ=1 AngleXU=0 Radius=0.4 StartAngle=4.72489 EndAngle=6.28319
    g270: LineSegment StartX=57 StartY=88.6487 StartZ=0 EndX=57 EndY=87.3325 EndZ=0
    g271: ArcOfCircle CenterX=19 CenterY=80.4127 CenterZ=0 NormalX=0 NormalY=0 NormalZ=1 AngleXU=0 Radius=2 StartAngle=3.14159 EndAngle=4.69989
    g272: ArcOfCircle CenterX=56.6 CenterY=76.2263 CenterZ=0 NormalX=0 NormalY=0 NormalZ=1 AngleXU=0 Radius=0.4 StartAngle=4.72489 EndAngle=6.28319
    g273: ArcOfCircle CenterX=19 CenterY=95.5686 CenterZ=0 NormalX=0 NormalY=0 NormalZ=1 AngleXU=0 Radius=2 StartAngle=1.5833 EndAngle=3.14159
    g274: ArcOfCircle CenterX=56.6 CenterY=22.0063 CenterZ=0 NormalX=0 NormalY=0 NormalZ=1 AngleXU=0 Radius=0.4 StartAngle=0 EndAngle=1.5708
    g275: ArcOfCircle CenterX=56.6 CenterY=77.5425 CenterZ=0 NormalX=0 NormalY=0 NormalZ=1 AngleXU=0 Radius=0.4 StartAngle=0 EndAngle=1.5583
    g276: ArcOfCircle CenterX=56.6 CenterY=55.33 CenterZ=0 NormalX=0 NormalY=0 NormalZ=1 AngleXU=0 Radius=0.4 StartAngle=0 EndAngle=1.5583
    g277: ArcOfCircle CenterX=56.6 CenterY=88.6487 CenterZ=0 NormalX=0 NormalY=0 NormalZ=1 AngleXU=0 Radius=0.4 StartAngle=0 EndAngle=1.5583
    g278: ArcOfCircle CenterX=19 CenterY=84.4623 CenterZ=0 NormalX=0 NormalY=0 NormalZ=1 AngleXU=0 Radius=2 StartAngle=1.5833 EndAngle=3.14159
    g279: ArcOfCircle CenterX=47.5 CenterY=7.93471 CenterZ=0 NormalX=0 NormalY=0 NormalZ=1 AngleXU=0 Radius=0.5 StartAngle=0 EndAngle=0.813169
    g280: ArcOfCircle CenterX=37.5146 CenterY=3.55 CenterZ=0 NormalX=0 NormalY=0 NormalZ=1 AngleXU=0 Radius=0.4 StartAngle=3.1679 EndAngle=4.71239
    g281: ArcOfCircle CenterX=36.2181 CenterY=18.6068 CenterZ=0 NormalX=0 NormalY=0 NormalZ=1 AngleXU=0 Radius=0.5 StartAngle=0.0263097 EndAngle=0.813169
    g282: ArcOfCircle CenterX=56.6 CenterY=33.1207 CenterZ=0 NormalX=0 NormalY=0 NormalZ=1 AngleXU=0 Radius=0.4 StartAngle=0 EndAngle=1.5502
    g283: ArcOfCircle CenterX=32.9614 CenterY=34.5078 CenterZ=0 NormalX=0 NormalY=0 NormalZ=1 AngleXU=0 Radius=0.5 StartAngle=3.84528 EndAngle=4.69179
    g284: ArcOfCircle CenterX=56.6 CenterY=20.6805 CenterZ=0 NormalX=0 NormalY=0 NormalZ=1 AngleXU=0 Radius=0.4 StartAngle=4.76235 EndAngle=6.28319
    g285: ArcOfCircle CenterX=30 CenterY=40.0467 CenterZ=0 NormalX=0 NormalY=0 NormalZ=1 AngleXU=0 Radius=2 StartAngle=1.58804 EndAngle=3.14159
    g286: ArcOfCircle CenterX=52.2315 CenterY=11.8 CenterZ=0 NormalX=0 NormalY=0 NormalZ=1 AngleXU=0 Radius=0.5 StartAngle=3.84528 EndAngle=4.71239
    g287: ArcOfCircle CenterX=42.8066 CenterY=22.9062 CenterZ=0 NormalX=0 NormalY=0 NormalZ=1 AngleXU=0 Radius=0.5 StartAngle=3.84528 EndAngle=4.71239
    g288: ArcOfCircle CenterX=37.5 CenterY=29.1595 CenterZ=0 NormalX=0 NormalY=0 NormalZ=1 AngleXU=0 Radius=0.5 StartAngle=3.14159 EndAngle=3.84528
    g289: ArcOfCircle CenterX=41.4025 CenterY=11.15 CenterZ=0 NormalX=0 NormalY=0 NormalZ=1 AngleXU=0 Radius=2 StartAngle=1.5708 EndAngle=3.09163
    g290: ArcOfCircle CenterX=48.4 CenterY=3.55 CenterZ=0 NormalX=0 NormalY=0 NormalZ=1 AngleXU=0 Radius=0.4 StartAngle=3.14159 EndAngle=4.71239
    g291: ArcOfCircle CenterX=39 CenterY=29.4062 CenterZ=0 NormalX=0 NormalY=0 NormalZ=1 AngleXU=0 Radius=2 StartAngle=1.5708 EndAngle=3.14159
    g292: ArcOfCircle CenterX=38.6195 CenterY=3.55 CenterZ=0 NormalX=0 NormalY=0 NormalZ=1 AngleXU=0 Radius=0.4 StartAngle=4.71239 EndAngle=6.23323
    g293: ArcOfCircle CenterX=56.6 CenterY=31.8062 CenterZ=0 NormalX=0 NormalY=0 NormalZ=1 AngleXU=0 Radius=0.4 StartAngle=4.71239 EndAngle=6.28319
    g294: ArcOfCircle CenterX=23.5626 CenterY=45.5832 CenterZ=0 NormalX=0 NormalY=0 NormalZ=1 AngleXU=0 Radius=0.5 StartAngle=3.84528 EndAngle=4.6985
    g295: ArcOfCircle CenterX=28.5 CenterY=39.765 CenterZ=0 NormalX=0 NormalY=0 NormalZ=1 AngleXU=0 Radius=0.5 StartAngle=3.14159 EndAngle=3.84528
    g296: ArcOfCircle CenterX=42.5153 CenterY=12.65 CenterZ=0 NormalX=0 NormalY=0 NormalZ=1 AngleXU=0 Radius=0.5 StartAngle=0.813169 EndAngle=1.5708
    g297: ArcOfCircle CenterX=26.6428 CenterY=3.55 CenterZ=0 NormalX=0 NormalY=0 NormalZ=1 AngleXU=0 Radius=0.4 StartAngle=3.15963 EndAngle=4.71239
    g298: ArcOfCircle CenterX=47.5 CenterY=17.3755 CenterZ=0 NormalX=0 NormalY=0 NormalZ=1 AngleXU=0 Radius=0.5 StartAngle=3.14159 EndAngle=3.84528
    g299: ArcOfCircle CenterX=56.6 CenterY=42.9057 CenterZ=0 NormalX=0 NormalY=0 NormalZ=1 AngleXU=0 Radius=0.4 StartAngle=4.72963 EndAngle=6.28319
    g300: ArcOfCircle CenterX=49 CenterY=17.8975 CenterZ=0 NormalX=0 NormalY=0 NormalZ=1 AngleXU=0 Radius=2 StartAngle=1.62075 EndAngle=3.14159
    g301: ArcOfCircle CenterX=27.7354 CenterY=3.55 CenterZ=0 NormalX=0 NormalY=0 NormalZ=1 AngleXU=0 Radius=0.4 StartAngle=4.71239 EndAngle=6.25688
    g302: ArcOfCircle CenterX=56.6 CenterY=44.2243 CenterZ=0 NormalX=0 NormalY=0 NormalZ=1 AngleXU=0 Radius=0.4 StartAngle=0 EndAngle=1.55691
    g303: ArcOfCircle CenterX=8.96899 CenterY=41.15 CenterZ=0 NormalX=0 NormalY=0 NormalZ=1 AngleXU=0 Radius=2 StartAngle=1.5708 EndAngle=3.12597
    g304: ArcOfCircle CenterX=21.3724 CenterY=32.65 CenterZ=0 NormalX=0 NormalY=0 NormalZ=1 AngleXU=0 Radius=0.5 StartAngle=0.813169 EndAngle=1.5708
    g305: ArcOfCircle CenterX=15.7713 CenterY=3.55 CenterZ=0 NormalX=0 NormalY=0 NormalZ=1 AngleXU=0 Radius=0.4 StartAngle=3.15097 EndAngle=4.71239
    g306: ArcOfCircle CenterX=25.2845 CenterY=28.9493 CenterZ=0 NormalX=0 NormalY=0 NormalZ=1 AngleXU=0 Radius=0.5 StartAngle=0.0180368 EndAngle=0.813169
    g307: ArcOfCircle CenterX=4.89503 CenterY=3.55 CenterZ=0 NormalX=0 NormalY=0 NormalZ=1 AngleXU=0 Radius=0.4 StartAngle=3.15409 EndAngle=4.71239
    g308: ArcOfCircle CenterX=19.7169 CenterY=31.15 CenterZ=0 NormalX=0 NormalY=0 NormalZ=1 AngleXU=0 Radius=2 StartAngle=1.5708 EndAngle=3.12493
    g309: ArcOfCircle CenterX=10.801 CenterY=42.65 CenterZ=0 NormalX=0 NormalY=0 NormalZ=1 AngleXU=0 Radius=0.5 StartAngle=0.813169 EndAngle=1.5708
    g310: ArcOfCircle CenterX=2.02484 CenterY=41.15 CenterZ=0 NormalX=0 NormalY=0 NormalZ=1 AngleXU=0 Radius=2 StartAngle=0.0124993 EndAngle=1.5708
    g311: ArcOfCircle CenterX=16.8566 CenterY=3.55 CenterZ=0 NormalX=0 NormalY=0 NormalZ=1 AngleXU=0 Radius=0.4 StartAngle=4.71239 EndAngle=6.26652
    g312: ArcOfCircle CenterX=30.5731 CenterY=20.15 CenterZ=0 NormalX=0 NormalY=0 NormalZ=1 AngleXU=0 Radius=2 StartAngle=1.5708 EndAngle=3.11528
    g313: ArcOfCircle CenterX=-16.8566 CenterY=3.55 CenterZ=0 NormalX=0 NormalY=0 NormalZ=1 AngleXU=0 Radius=0.4 StartAngle=3.15826 EndAngle=4.71239
    g314: ArcOfCircle CenterX=-8.96899 CenterY=41.15 CenterZ=0 NormalX=0 NormalY=0 NormalZ=1 AngleXU=0 Radius=2 StartAngle=0.0156237 EndAngle=1.5708
    g315: ArcOfCircle CenterX=-4.89503 CenterY=3.55 CenterZ=0 NormalX=0 NormalY=0 NormalZ=1 AngleXU=0 Radius=0.4 StartAngle=4.71239 EndAngle=6.27069
    g316: ArcOfCircle CenterX=-14.5376 CenterY=39.1154 CenterZ=0 NormalX=0 NormalY=0 NormalZ=1 AngleXU=0 Radius=0.5 StartAngle=2.32842 EndAngle=3.13221
    g317: ArcOfCircle CenterX=-15.7713 CenterY=3.55 CenterZ=0 NormalX=0 NormalY=0 NormalZ=1 AngleXU=0 Radius=0.4 StartAngle=4.71239 EndAngle=6.2738
    g318: ArcOfCircle CenterX=-2.02484 CenterY=41.15 CenterZ=0 NormalX=0 NormalY=0 NormalZ=1 AngleXU=0 Radius=2 StartAngle=1.5708 EndAngle=3.12909
    g319: ArcOfCircle CenterX=14.5376 CenterY=39.1154 CenterZ=0 NormalX=0 NormalY=0 NormalZ=1 AngleXU=0 Radius=0.5 StartAngle=0.00938155 EndAngle=0.813169
    g320: ArcOfCircle CenterX=33.001 CenterY=21.65 CenterZ=0 NormalX=0 NormalY=0 NormalZ=1 AngleXU=0 Radius=0.5 StartAngle=0.813169 EndAngle=1.5708
    g321: ArcOfCircle CenterX=5.9812 CenterY=3.55 CenterZ=0 NormalX=0 NormalY=0 NormalZ=1 AngleXU=0 Radius=0.4 StartAngle=4.71239 EndAngle=6.26756
    g322: ArcOfCircle CenterX=-56.6 CenterY=20.6805 CenterZ=0 NormalX=0 NormalY=0 NormalZ=1 AngleXU=0 Radius=0.4 StartAngle=3.14159 EndAngle=4.66243
    g323: ArcOfCircle CenterX=-37.5 CenterY=29.1595 CenterZ=0 NormalX=0 NormalY=0 NormalZ=1 AngleXU=0 Radius=0.5 StartAngle=5.5795 EndAngle=6.28319
    g324: ArcOfCircle CenterX=-10.801 CenterY=42.65 CenterZ=0 NormalX=0 NormalY=0 NormalZ=1 AngleXU=0 Radius=0.5 StartAngle=1.5708 EndAngle=2.32842
    g325: ArcOfCircle CenterX=-33.001 CenterY=21.65 CenterZ=0 NormalX=0 NormalY=0 NormalZ=1 AngleXU=0 Radius=0.5 StartAngle=1.5708 EndAngle=2.32842
    g326: ArcOfCircle CenterX=-5.9812 CenterY=3.55 CenterZ=0 NormalX=0 NormalY=0 NormalZ=1 AngleXU=0 Radius=0.4 StartAngle=3.15722 EndAngle=4.71239
    g327: ArcOfCircle CenterX=-42.8066 CenterY=22.9062 CenterZ=0 NormalX=0 NormalY=0 NormalZ=1 AngleXU=0 Radius=0.5 StartAngle=4.71239 EndAngle=5.5795
    g328: ArcOfCircle CenterX=-56.6 CenterY=22.0063 CenterZ=0 NormalX=0 NormalY=0 NormalZ=1 AngleXU=0 Radius=0.4 StartAngle=1.5708 EndAngle=3.14159
    g329: ArcOfCircle CenterX=-39 CenterY=29.4062 CenterZ=0 NormalX=0 NormalY=0 NormalZ=1 AngleXU=0 Radius=2 StartAngle=0 EndAngle=1.5708
    g330: ArcOfCircle CenterX=-38.6195 CenterY=3.55 CenterZ=0 NormalX=0 NormalY=0 NormalZ=1 AngleXU=0 Radius=0.4 StartAngle=3.19155 EndAngle=4.71239
    g331: ArcOfCircle CenterX=-19.7169 CenterY=31.15 CenterZ=0 NormalX=0 NormalY=0 NormalZ=1 AngleXU=0 Radius=2 StartAngle=0.0166651 EndAngle=1.5708
    g332: ArcOfCircle CenterX=-47.5 CenterY=17.3755 CenterZ=0 NormalX=0 NormalY=0 NormalZ=1 AngleXU=0 Radius=0.5 StartAngle=5.5795 EndAngle=6.28319
    g333: ArcOfCircle CenterX=-56.6 CenterY=31.8062 CenterZ=0 NormalX=0 NormalY=0 NormalZ=1 AngleXU=0 Radius=0.4 StartAngle=3.14159 EndAngle=4.71239
    g334: ArcOfCircle CenterX=-25.2845 CenterY=28.9493 CenterZ=0 NormalX=0 NormalY=0 NormalZ=1 AngleXU=0 Radius=0.5 StartAngle=2.32842 EndAngle=3.12356
    g335: ArcOfCircle CenterX=-37.5146 CenterY=3.55 CenterZ=0 NormalX=0 NormalY=0 NormalZ=1 AngleXU=0 Radius=0.4 StartAngle=4.71239 EndAngle=6.25688
    g336: ArcOfCircle CenterX=-21.3724 CenterY=32.65 CenterZ=0 NormalX=0 NormalY=0 NormalZ=1 AngleXU=0 Radius=0.5 StartAngle=1.5708 EndAngle=2.32842
    g337: ArcOfCircle CenterX=-26.6428 CenterY=3.55 CenterZ=0 NormalX=0 NormalY=0 NormalZ=1 AngleXU=0 Radius=0.4 StartAngle=4.71239 EndAngle=6.26515
    g338: ArcOfCircle CenterX=-48.4 CenterY=3.55 CenterZ=0 NormalX=0 NormalY=0 NormalZ=1 AngleXU=0 Radius=0.4 StartAngle=4.71239 EndAngle=6.28319
    g339: ArcOfCircle CenterX=-36.2181 CenterY=18.6068 CenterZ=0 NormalX=0 NormalY=0 NormalZ=1 AngleXU=0 Radius=0.5 StartAngle=2.32842 EndAngle=3.11528
    g340: ArcOfCircle CenterX=-27.7354 CenterY=3.55 CenterZ=0 NormalX=0 NormalY=0 NormalZ=1 AngleXU=0 Radius=0.4 StartAngle=3.1679 EndAngle=4.71239
    g341: ArcOfCircle CenterX=-30.5731 CenterY=20.15 CenterZ=0 NormalX=0 NormalY=0 NormalZ=1 AngleXU=0 Radius=2 StartAngle=0.0263097 EndAngle=1.5708
    g342: ArcOfCircle CenterX=-42.5153 CenterY=12.65 CenterZ=0 NormalX=0 NormalY=0 NormalZ=1 AngleXU=0 Radius=0.5 StartAngle=1.5708 EndAngle=2.32842
    g343: ArcOfCircle CenterX=-41.4025 CenterY=11.15 CenterZ=0 NormalX=0 NormalY=0 NormalZ=1 AngleXU=0 Radius=2 StartAngle=0.0499584 EndAngle=1.5708
    g344: ArcOfCircle CenterX=-47.5 CenterY=7.93471 CenterZ=0 NormalX=0 NormalY=0 NormalZ=1 AngleXU=0 Radius=0.5 StartAngle=2.32842 EndAngle=3.14159
    g345: LineSegment StartX=17 StartY=62.2498 StartZ=0 EndX=17 EndY=58.2002 EndZ=0
    g346: ArcOfCircle CenterX=-52.2315 CenterY=11.8 CenterZ=0 NormalX=0 NormalY=0 NormalZ=1 AngleXU=0 Radius=0.5 StartAngle=4.71239 EndAngle=5.5795
    g347: ArcOfCircle CenterX=-49 CenterY=17.8975 CenterZ=0 NormalX=0 NormalY=0 NormalZ=1 AngleXU=0 Radius=2 StartAngle=0 EndAngle=1.52084
FEATURE [PartDesign::Pad] Pad
  Length = 120
  Length2 = 100
  Profile = -> Sketch348
  Refine = true
  Type = 0
FEATURE [PartDesign::Body] Body
  Group = -> [Sketch348,Pad]
  Origin = -> Origin001
  Tip = -> Pad
FEATURE [App::Part] Part
  Group = -> [Body]
  License = CC BY 3.0
  LicenseURL = http://creativecommons.org/licenses/by/3.0/
  Origin = -> Origin
